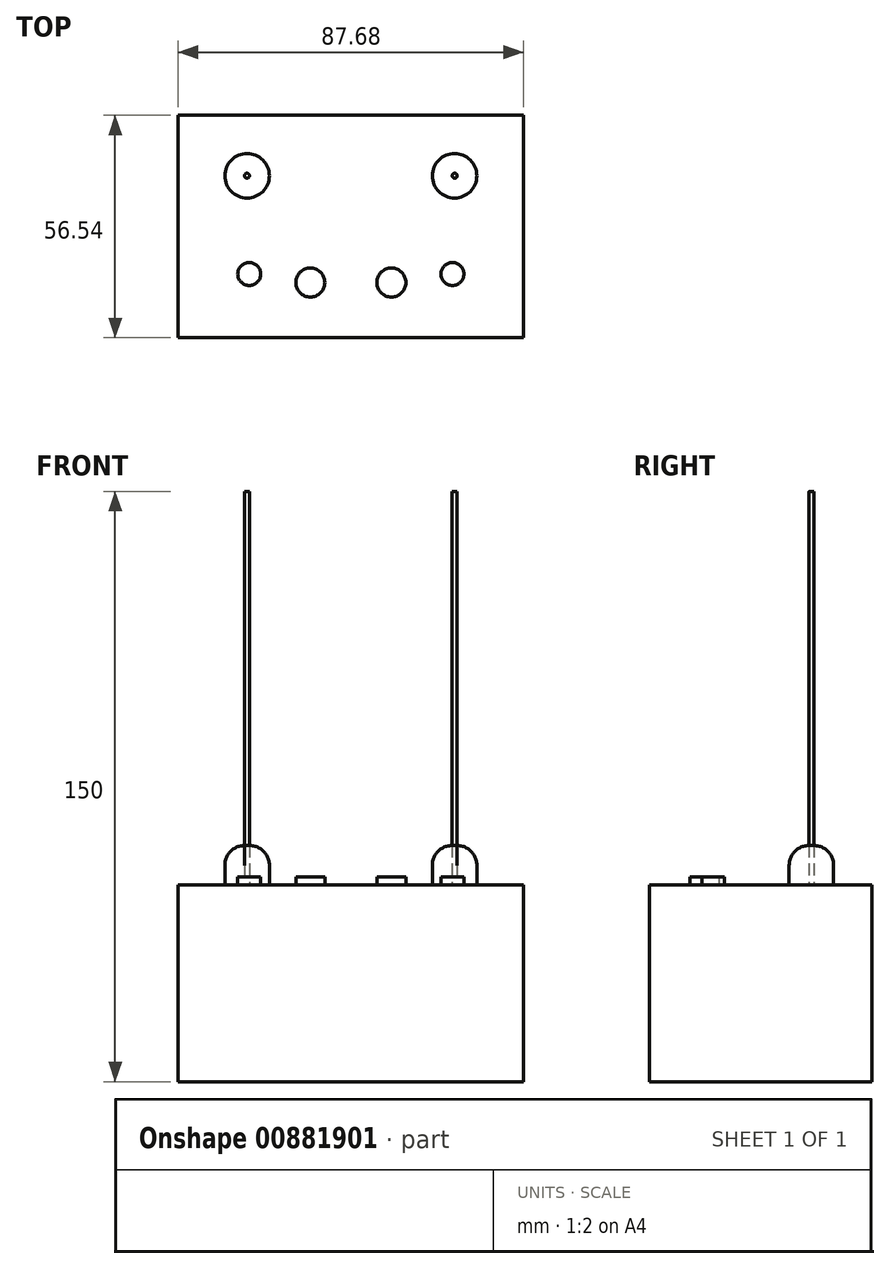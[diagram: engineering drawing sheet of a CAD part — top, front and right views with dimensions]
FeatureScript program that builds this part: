
annotation { "Feature Type Name" : "Feature", "Feature Type Description" : "" }
export const myFeature = defineFeature(function(context is Context, id is Id, definition is map)
    precondition{}
    {
        {
            var Q0;
            Q0=qCreatedBy(makeId("Top.planeOp"),FACE);
            var sketch = newSketch(context, id + "F0", { "sketchPlane" : qUnion([Q0])});
            skLineSegment(sketch, "E0.bottom", {"start": v(-43.84, 28.27) * mm, "end": v(43.84, 28.27) * mm});
            skLineSegment(sketch, "E0.top", {"start": v(-43.84, -28.27) * mm, "end": v(43.84, -28.27) * mm});
            skLineSegment(sketch, "E0.left", {"start": v(-43.84, 28.27) * mm, "end": v(-43.84, -28.27) * mm});
            skLineSegment(sketch, "E0.right", {"start": v(43.84, 28.27) * mm, "end": v(43.84, -28.27) * mm});
            skPoint(sketch, "E0.middle", {"position": v(0, 0) * mm});
            skSolve(sketch);
        }
        {
            var Q0;
            Q0 = qSketchRegion(id + "F0", true);
            extrude(context, id + "F1", {"entities" : qUnion([Q0]), "depth" : 50 * mm, "offsetDistance" : 25 * mm});
        }
        {
            var Q0;
            Q0=makeQuery(id+"F1.opExtrude","CAP_FACE",FACE,{"disambiguationData":[OSD([sQuery(id+"F0.wireOp",EDGE,"E0.bottom"),sQuery(id+"F0.wireOp",EDGE,"E0.top"),sQuery(id+"F0.wireOp",EDGE,"E0.left"),sQuery(id+"F0.wireOp",EDGE,"E0.right")])],"isStart":false});
            var sketch = newSketch(context, id + "F2", { "sketchPlane" : qUnion([Q0])});
            skCircle(sketch, "E1", {"center": v(-26.35, 12.9) * mm, "radius": 5.66 * mm});
            skCircle(sketch, "E2.MirrorC", {"center": v(26.35, 12.9) * mm, "radius": 5.66 * mm});
            skSolve(sketch);
        }
        {
            var Q0;
            Q0 = qSketchRegion(id + "F2", true);
            extrude(context, id + "F3", {"entities" : qUnion([Q0]), "depth" : 10 * mm, "offsetDistance" : 25 * mm});
        }
        {
            var Q0;
            Q0=makeQuery(id+"F1.opExtrude","CAP_FACE",FACE,{"disambiguationData":[OSD([sQuery(id+"F0.wireOp",EDGE,"E0.bottom"),sQuery(id+"F0.wireOp",EDGE,"E0.top"),sQuery(id+"F0.wireOp",EDGE,"E0.left"),sQuery(id+"F0.wireOp",EDGE,"E0.right")])],"isStart":false});
            var sketch = newSketch(context, id + "F4", { "sketchPlane" : qUnion([Q0])});
            skCircle(sketch, "E3", {"center": v(-25.81, -12.06) * mm, "radius": 2.91 * mm});
            skCircle(sketch, "E4", {"center": v(-10.3, -14.23) * mm, "radius": 3.68 * mm});
            skCircle(sketch, "E5.MirrorC", {"center": v(10.3, -14.23) * mm, "radius": 3.68 * mm});
            skCircle(sketch, "E6.MirrorC", {"center": v(25.81, -12.06) * mm, "radius": 2.91 * mm});
            skSolve(sketch);
        }
        {
            var Q0;
            Q0 = qSketchRegion(id + "F4", true);
            extrude(context, id + "F5", {"entities" : qUnion([Q0]), "depth" : 2 * mm, "offsetDistance" : 25 * mm});
        }
        {
            var Q0;
            Q0=makeQuery(id+"F3.opExtrude","CAP_EDGE",EDGE,{"disambiguationData":[OSD([sQuery(id+"F2.wireOp",EDGE,"E2.MirrorC")])],"isStart":false});
            var Q1;
            Q1=makeQuery(id+"F3.opExtrude","CAP_EDGE",EDGE,{"disambiguationData":[OSD([sQuery(id+"F2.wireOp",EDGE,"E1")])],"isStart":false});
            fillet(context, id + "F6", {"entities" : qUnion([Q0, Q1]), "radius" : 5 * mm, "tangentPropagation" : true, "allowEdgeOverflow" : false});
        }
        {
            var Q0;
            Q0=makeQuery(id+"F1.opExtrude","CAP_FACE",FACE,{"disambiguationData":[OSD([sQuery(id+"F0.wireOp",EDGE,"E0.bottom"),sQuery(id+"F0.wireOp",EDGE,"E0.top"),sQuery(id+"F0.wireOp",EDGE,"E0.left"),sQuery(id+"F0.wireOp",EDGE,"E0.right")])],"isStart":false});
            var sketch = newSketch(context, id + "F7", { "sketchPlane" : qUnion([Q0])});
            skCircle(sketch, "E7", {"center": v(-26.38, 12.9) * mm, "radius": 0.63 * mm});
            skCircle(sketch, "E8.MirrorC", {"center": v(26.38, 12.9) * mm, "radius": 0.63 * mm});
            skSolve(sketch);
        }
        {
            var Q0;
            Q0 = qSketchRegion(id + "F7", true);
            extrude(context, id + "F8", {"entities" : qUnion([Q0]), "depth" : 100 * mm, "offsetDistance" : 25 * mm});
        }
    });
